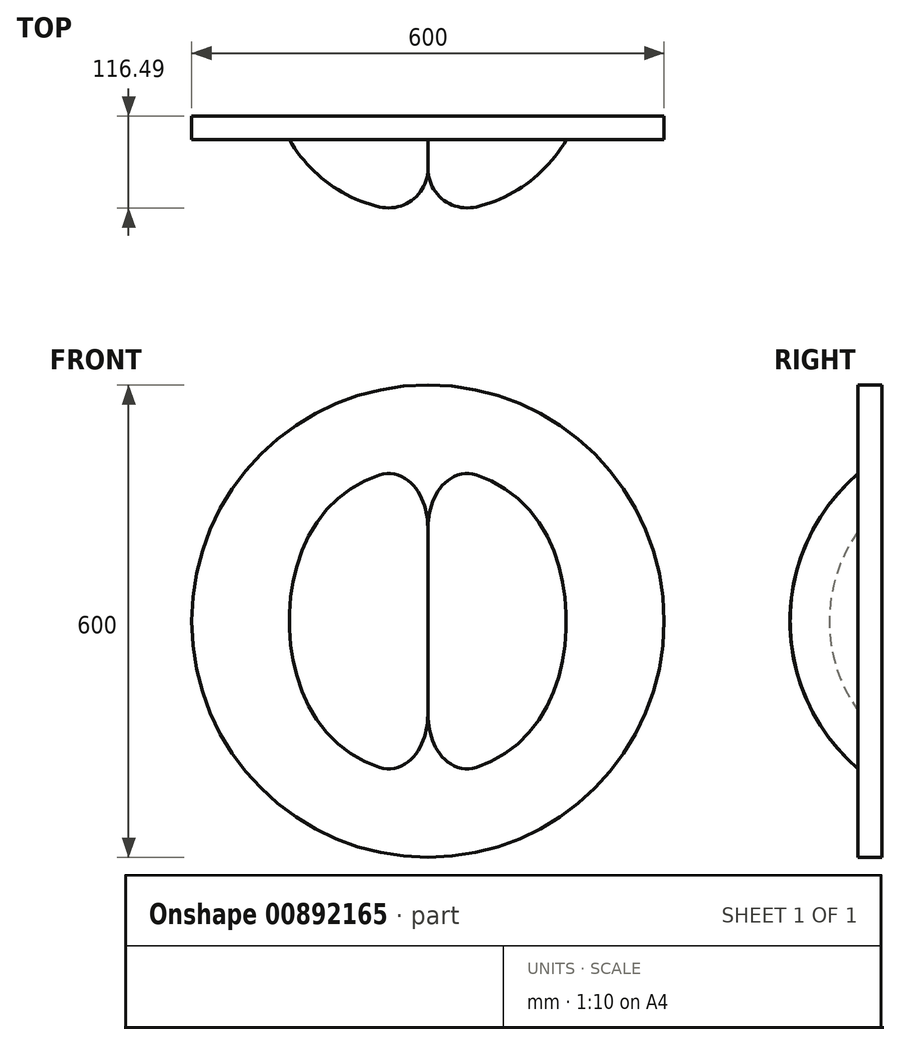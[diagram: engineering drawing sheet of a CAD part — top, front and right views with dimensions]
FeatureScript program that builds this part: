
annotation { "Feature Type Name" : "Feature", "Feature Type Description" : "" }
export const myFeature = defineFeature(function(context is Context, id is Id, definition is map)
    precondition{}
    {
        {
            var Q0;
            Q0=qCreatedBy(makeId("Front.planeOp"),FACE);
            cPlane(context, id + "F0", {"entities" : qUnion([Q0]), "cplaneType" : CPlaneType.OFFSET, "offset" : 160 * mm, "width" : 150 * mm, "height" : 150 * mm});
        }
        {
            var Q0;
            Q0=qCreatedBy(makeId("Right.planeOp"),FACE);
            cPlane(context, id + "F1", {"entities" : qUnion([Q0]), "cplaneType" : CPlaneType.OFFSET, "offset" : 10 * mm, "width" : 150 * mm, "height" : 150 * mm});
        }
        {
            var Q0;
            Q0=qCreatedBy(makeId("Right.planeOp"),FACE);
            var sketch = newSketch(context, id + "F2", { "sketchPlane" : qUnion([Q0])});
            skCircle(sketch, "E0", {"center": v(0, 0) * mm, "radius": 250 * mm});
            skSolve(sketch);
        }
        {
            var Q0;
            Q0=makeQuery(id+"F2.imprint","IMPRINT",FACE,{"disambiguationData":[TD([[makeQuery(id+"F2.imprint","IMPRINT",EDGE,{"derivedFrom":sQuery(id+"F2.wireOp",EDGE,"E0")}),1.0]])]});
            extrude(context, id + "F3", {"entities" : qUnion([Q0]), "depth" : 200 * mm, "offsetDistance" : 25 * mm});
        }
        {
            var Q0;
            Q0=makeQuery(id+"F3.opExtrude","CAP_EDGE",EDGE,{"disambiguationData":[OSD([sQuery(id+"F2.wireOp",EDGE,"E0")])],"isStart":false});
            fillet(context, id + "F4", {"entities" : qUnion([Q0]), "radius" : 180 * mm, "tangentPropagation" : true, "allowEdgeOverflow" : false});
        }
        {
            var Q0;
            Q0=makeQuery(id+"F7.boolean.opBoolean","MERGE",FACE,{"derivedFrom":[makeQuery(id+"F3.opExtrude","SWEPT_FACE",FACE,{"disambiguationData":[OSD([sQuery(id+"F2.wireOp",EDGE,"E0")])]}),makeQuery(id+"F7.opExtrude","SWEPT_FACE",FACE,{"disambiguationData":[OSD([sQuery(id+"F6.wireOp",EDGE,"E1")])]})]});
            fillet(context, id + "F5", {"entities" : qUnion([Q0]), "radius" : 50 * mm, "tangentPropagation" : true, "allowEdgeOverflow" : false});
        }
        {
            var Q0;
            Q0=qCreatedBy(makeId("Right.planeOp"),FACE);
            var sketch = newSketch(context, id + "F6", { "sketchPlane" : qUnion([Q0])});
            skCircle(sketch, "E1", {"center": v(0, 0) * mm, "radius": 250 * mm});
            skSolve(sketch);
        }
        {
            var Q0;
            Q0=qSketchRegion(id+"F6",true);
            extrude(context, id + "F7", {"entities" : qUnion([Q0]), "oppositeDirection" : true, "depth" : 200 * mm, "offsetDistance" : 25 * mm});
        }
        {
            var Q0;
            Q0=makeQuery(id+"F7.opExtrude","CAP_EDGE",EDGE,{"disambiguationData":[OSD([sQuery(id+"F6.wireOp",EDGE,"E1")])],"isStart":false});
            fillet(context, id + "F8", {"entities" : qUnion([Q0]), "radius" : 180 * mm, "tangentPropagation" : true, "allowEdgeOverflow" : false});
        }
        {
            var Q0;
            Q0=makeQuery(id+"F7.opExtrude","SWEPT_FACE",FACE,{"disambiguationData":[OSD([sQuery(id+"F6.wireOp",EDGE,"E1")])]});
            fillet(context, id + "F9", {"entities" : qUnion([Q0]), "radius" : 50 * mm, "tangentPropagation" : true, "allowEdgeOverflow" : false});
        }
        {
            var Q0;
            Q0=qCreatedBy(id+"F0.planeOp",FACE);
            var sketch = newSketch(context, id + "F10", { "sketchPlane" : qUnion([Q0])});
            skCircle(sketch, "E2", {"center": v(0, 0) * mm, "radius": 200 * mm});
            skSolve(sketch);
        }
        {
            var Q0;
            Q0=qSketchRegion(id+"F10",true);
            extrude(context, id + "F11", {"entities" : qUnion([Q0]), "oppositeDirection" : true, "depth" : 105 * mm, "offsetDistance" : 25 * mm});
        }
        {
            var Q0;
            Q0=qCreatedBy(makeId("Right.planeOp"),FACE);
            var sketch = newSketch(context, id + "F12", { "sketchPlane" : qUnion([Q0])});
            skCircle(sketch, "E3", {"center": v(-160, 270) * mm, "radius": 5 * mm});
            skSolve(sketch);
        }
        {
            var Q0;
            Q0=qCreatedBy(id+"F0.planeOp",FACE);
            var sketch = newSketch(context, id + "F13", { "sketchPlane" : qUnion([Q0])});
            skCircle(sketch, "E4", {"center": v(0, 0) * mm, "radius": 360 * mm});
            skSolve(sketch);
        }
        {
            var Q0;
            Q0=makeQuery(id+"F13.imprint","IMPRINT",FACE,{"disambiguationData":[TD([[makeQuery(id+"F13.imprint","IMPRINT",EDGE,{"derivedFrom":sQuery(id+"F13.wireOp",EDGE,"E4")}),1.0]])]});
            extrude(context, id + "F14", {"entities" : qUnion([Q0]), "operationType" : NewBodyOperationType.REMOVE, "oppositeDirection" : true, "depth" : 433 * mm, "offsetDistance" : 25 * mm});
        }
        {
            var Q0;
            Q0=qCreatedBy(id+"F0.planeOp",FACE);
            var sketch = newSketch(context, id + "F15", { "sketchPlane" : qUnion([Q0])});
            skCircle(sketch, "E5", {"center": v(0, 0) * mm, "radius": 300 * mm});
            skSolve(sketch);
        }
        {
            var Q0;
            Q0=makeQuery(id+"F15.imprint","IMPRINT",FACE,{"disambiguationData":[TD([[makeQuery(id+"F15.imprint","IMPRINT",EDGE,{"derivedFrom":sQuery(id+"F15.wireOp",EDGE,"E5")}),1.0]])]});
            extrude(context, id + "F16", {"entities" : qUnion([Q0]), "operationType" : NewBodyOperationType.ADD, "oppositeDirection" : true, "depth" : 30 * mm, "offsetDistance" : 25 * mm});
        }
    });
